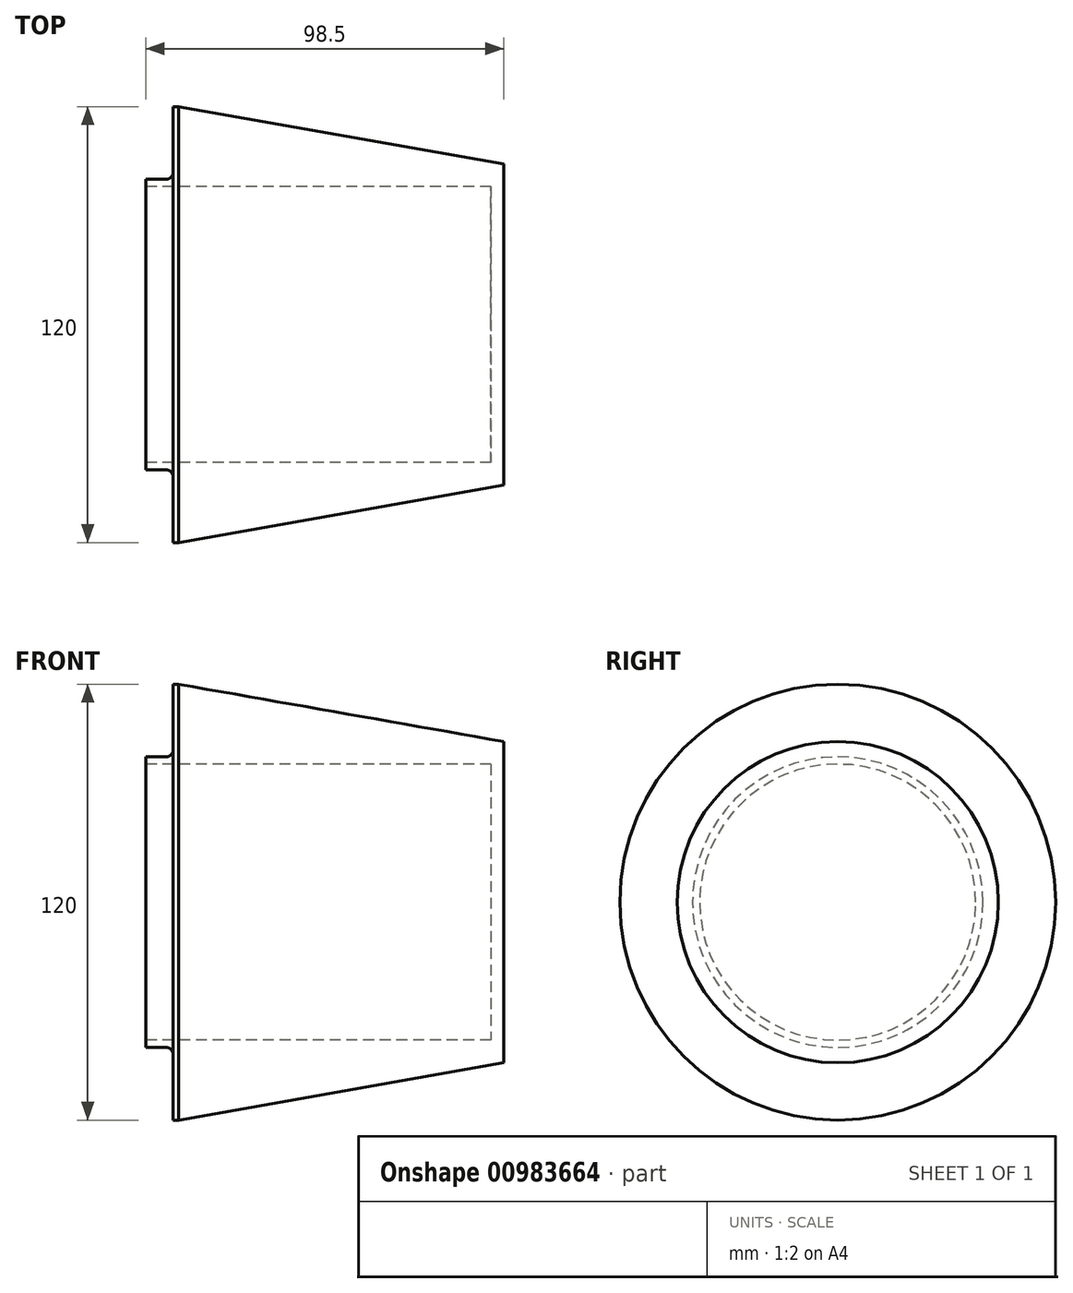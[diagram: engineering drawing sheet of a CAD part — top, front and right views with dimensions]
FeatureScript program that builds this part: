
annotation { "Feature Type Name" : "Feature", "Feature Type Description" : "" }
export const myFeature = defineFeature(function(context is Context, id is Id, definition is map)
    precondition{}
    {
        {
            var Q0;
            Q0=qCreatedBy(makeId("Front.planeOp"),FACE);
            var sketch = newSketch(context, id + "F0", { "sketchPlane" : qUnion([Q0])});
            skLineSegment(sketch, "E0.bottom", {"start": v(0, 0) * mm, "end": v(100, 0) * mm});
            skLineSegment(sketch, "E0.left", {"start": v(0, 0) * mm, "end": v(0, 40) * mm});
            skLineSegment(sketch, "E0.right", {"start": v(100, 0) * mm, "end": v(100, 43.95) * mm});
            skLineSegment(sketch, "E1", {"start": v(0, 40) * mm, "end": v(5.5, 40) * mm});
            skLineSegment(sketch, "E2", {"start": v(7.5, 42) * mm, "end": v(7.5, 60) * mm});
            skPoint(sketch, "E3.visualSharp", {"position": v(7.5, 40) * mm});
            skArc(sketch, "E3.filletArc", {"start": v(5.5, 40) * mm, "mid": v(6.91, 40.59) * mm, "end": v(7.5, 42) * mm});
            skLineSegment(sketch, "E4", {"start": v(7.5, 42) * mm, "end": v(7.5, 0) * mm});
            skLineSegment(sketch, "E5.bottom", {"start": v(7.5, 60) * mm, "end": v(9, 60) * mm});
            skLineSegment(sketch, "E5.top", {"start": v(7.5, 0) * mm, "end": v(9, 0) * mm});
            skLineSegment(sketch, "E5.left", {"start": v(7.5, 60) * mm, "end": v(7.5, 0) * mm});
            skLineSegment(sketch, "E5.right", {"start": v(9, 60) * mm, "end": v(9, 0) * mm});
            skLineSegment(sketch, "E6", {"start": v(9, 60) * mm, "end": v(100, 43.95) * mm});
            skLineSegment(sketch, "E7", {"start": v(-27.56, 0) * mm, "end": v(121.24, 0) * mm, "construction": true});
            skLineSegment(sketch, "E8", {"start": v(98.5, 44.22) * mm, "end": v(98.5, 0) * mm});
            skLineSegment(sketch, "E9.bottom", {"start": v(98.5, 0) * mm, "end": v(100, 0) * mm});
            skLineSegment(sketch, "E9.top", {"start": v(98.5, 43.95) * mm, "end": v(100, 43.95) * mm});
            skLineSegment(sketch, "E9.left", {"start": v(98.5, 0) * mm, "end": v(98.5, 43.95) * mm});
            skSolve(sketch);
        }
        {
            var Q0;
            {var subQ0=sQuery(id+"F0.wireOp",EDGE,"E0.left");Q0=makeQuery(id+"F0.imprint","IMPRINT",FACE,{"disambiguationData":[TD([[makeQuery(id+"F0.imprint","IMPRINT",EDGE,{"derivedFrom":subQ0}),-1.0]])]});}
            var Q1;
            {var subQ5=sQuery(id+"F0.wireOp",EDGE,"E5.right");Q1=makeQuery(id+"F0.imprint","IMPRINT",FACE,{"disambiguationData":[TD([[makeQuery(id+"F0.imprint","IMPRINT",EDGE,{"derivedFrom":subQ5}),1.0]])]});}
            var Q2;
            {var subQ0=sQuery(id+"F0.wireOp",EDGE,"E0.right");Q2=makeQuery(id+"F0.imprint","IMPRINT",FACE,{"disambiguationData":[TD([[makeQuery(id+"F0.imprint","IMPRINT",EDGE,{"derivedFrom":subQ0}),1.0]])]});}
            var Q3;
            Q3=makeQuery(id+"F0.imprint","IMPRINT",FACE,{"disambiguationData":[TD([[makeQuery(id+"F0.imprint","IMPRINT",EDGE,{"derivedFrom":sQuery(id+"F0.wireOp",EDGE,"E2")}),-1.0]])]});
            var Q4;
            Q4=sQuery(id+"F0.wireOp",EDGE,"E7");
            revolve(context, id + "F1", {"surfaceOperationType" : NewSurfaceOperationType.NEW, "entities" : qUnion([Q0, Q1, Q2, Q3]), "axis" : qUnion([Q4]), "revolveType" : RevolveType.FULL});
        }
        {
            var Q0;
            Q0=makeQuery(id+"F1.opRevolve","SWEPT_FACE",FACE,{"disambiguationData":[OSD([sQuery(id+"F0.wireOp",EDGE,"E0.left")])]});
            var sketch = newSketch(context, id + "F2", { "sketchPlane" : qUnion([Q0])});
            skCircle(sketch, "E10", {"center": v(0, 0) * mm, "radius": 38 * mm});
            skSolve(sketch);
        }
        {
            var Q0;
            Q0=makeQuery(id+"F2.imprint","IMPRINT",FACE,{"disambiguationData":[TD([[makeQuery(id+"F2.imprint","IMPRINT",EDGE,{"derivedFrom":sQuery(id+"F2.wireOp",EDGE,"E10")}),1.0]])]});
            extrude(context, id + "F3", {"entities" : qUnion([Q0]), "operationType" : NewBodyOperationType.REMOVE, "oppositeDirection" : true, "depth" : 95 * mm, "offsetDistance" : 25 * mm});
        }
    });
